# Revit family: Outdoor-Kitchen-Cabinets_Kalamazoo_Appliance-Back-Panels_Arcadia
name_source: partatom
category: Specialty Equipment
revit_build: Autodesk Revit 2018 (Build: 20190510_1515(x64)
units: mm (PartAtom-declared; Revit-internal decimal feet)

## family parameters
Always vertical = Yes
Cut with Voids When Loaded = No
OmniClass Number = 23.40.40.11
OmniClass Title = Specialized Food Storage and Display Furnishings
Part Type = Normal
Room Calculation Point = No
Round Connector Dimension = Use Diameter
Shared = No
Work Plane-Based = No

## types (5) — shared parameters
Assembly Code = E1090300
Depth = 3 1/2"
Keynote = 11400
Manufacturer = Kalamazoo Outdoor Gourmet
Product Material = Kalamazoo - Stainless Steel - 304 OR 316L
Product data url = https://www.bimobject.com
URL = https://kalamazoogourmet.com
Ι_Gnrc Mdl Optn 01 = Extension : +3/4"
Ι_Gnrc Mdl Optn 02 = Extension : -3/4"

## per-type parameters (varying)
| type | Description | Weight (lb) | Width |
| KD-ABK-15 | Arcadia 15-Inch Appliance Back Panel | 150.00 lbf | 15" |
| KD-ABK-24 | Arcadia 24-Inch Appliance Back Panel | 170.00 lbf | 24" |
| KD-ABK-30 | Arcadia 30-Inch Appliance Back Panel | 180.00 lbf | 30" |
| KD-ABK-39 | Arcadia 39-Inch Appliance Back Panel | 190.00 lbf | 39" |
| KD-ABK-48 | Arcadia 48-Inch Appliance Back Panel | 200.00 lbf | 48" |

note: column(s) folded — value = type name in every type: Model

## geometry (parser evidence)
native form markers: Sweep x4
no freeform markers — native parametric forms only
